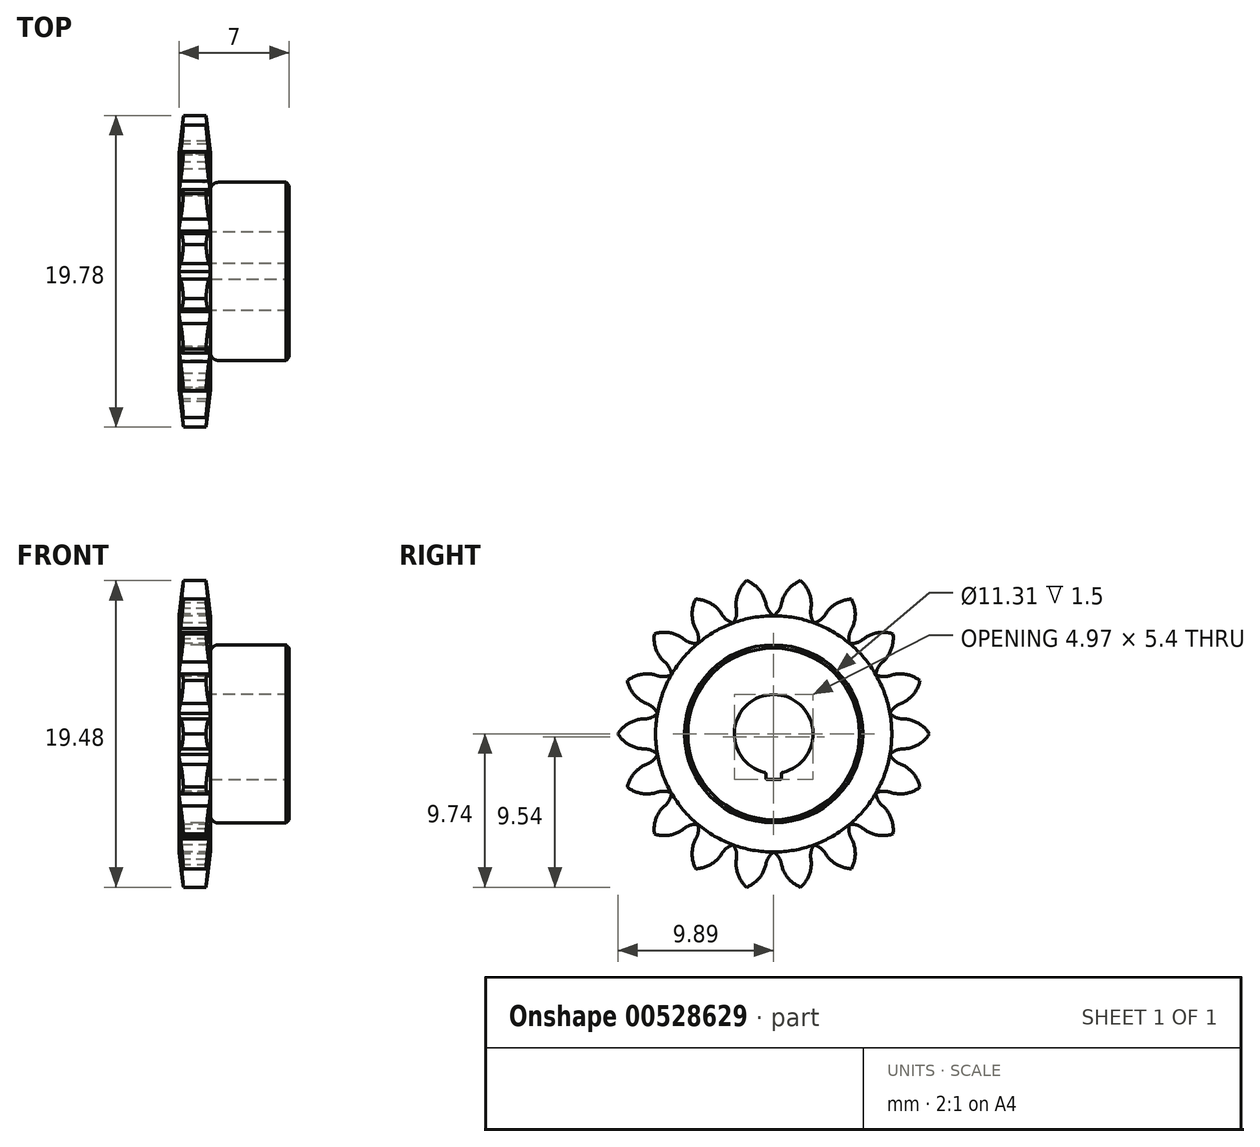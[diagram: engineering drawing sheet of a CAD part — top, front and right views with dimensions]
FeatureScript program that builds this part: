
annotation { "Feature Type Name" : "Feature", "Feature Type Description" : "" }
export const myFeature = defineFeature(function(context is Context, id is Id, definition is map)
    precondition{}
    {
        {
            var Q0;
            Q0=qCreatedBy(makeId("Front.planeOp"),FACE);
            var sketch = newSketch(context, id + "F0", { "sketchPlane" : qUnion([Q0])});
            skLineSegment(sketch, "E0", {"start": v(0, 0) * mm, "end": v(21.65, 0) * mm, "construction": true});
            skLineSegment(sketch, "E1.bottom", {"start": v(0, 10) * mm, "end": v(2, 10) * mm});
            skLineSegment(sketch, "E1.top", {"start": v(0, 2.5) * mm, "end": v(2, 2.5) * mm});
            skLineSegment(sketch, "E1.left", {"start": v(0, 10) * mm, "end": v(0, 2.5) * mm});
            skLineSegment(sketch, "E1.right", {"start": v(2, 10) * mm, "end": v(2, 2.5) * mm});
            skLineSegment(sketch, "E2.bottom", {"start": v(0, 2.5) * mm, "end": v(7, 2.5) * mm});
            skLineSegment(sketch, "E2.top", {"start": v(0, 5.66) * mm, "end": v(7, 5.66) * mm});
            skLineSegment(sketch, "E2.left", {"start": v(0, 2.5) * mm, "end": v(0, 5.66) * mm});
            skLineSegment(sketch, "E2.right", {"start": v(7, 2.5) * mm, "end": v(7, 5.66) * mm});
            skSolve(sketch);
        }
        {
            var Q0;
            {var subQ0=sQuery(id+"F0.wireOp",EDGE,"E1.bottom");Q0=makeQuery(id+"F0.imprint","IMPRINT",FACE,{"disambiguationData":[TD([[makeQuery(id+"F0.imprint","IMPRINT",EDGE,{"derivedFrom":subQ0}),-1.0]])]});}
            var Q1;
            {var subQ5=sQuery(id+"F0.wireOp",EDGE,"E2.right");Q1=makeQuery(id+"F0.imprint","IMPRINT",FACE,{"disambiguationData":[TD([[makeQuery(id+"F0.imprint","IMPRINT",EDGE,{"derivedFrom":subQ5}),1.0]])]});}
            var Q2;
            {var subQ5=sQuery(id+"F0.wireOp",EDGE,"E2.left");Q2=makeQuery(id+"F0.imprint","IMPRINT",FACE,{"disambiguationData":[TD([[makeQuery(id+"F0.imprint","IMPRINT",EDGE,{"derivedFrom":subQ5}),-1.0]])]});}
            var Q3;
            Q3=sQuery(id+"F0.wireOp",EDGE,"E0");
            revolve(context, id + "F1", {"entities" : qUnion([Q0, Q1, Q2]), "axis" : qUnion([Q3]), "revolveType" : RevolveType.FULL});
        }
        {
            var Q0;
            Q0=makeQuery(id+"F1.opRevolve","SWEPT_EDGE",EDGE,{"disambiguationData":[OSD([sQuery(id+"F0.wireOp",EDGE,"E1.right"),sQuery(id+"F0.wireOp",EDGE,"E2.top")])]});
            fillet(context, id + "F2", {"entities" : qUnion([Q0]), "radius" : .5 * mm, "tangentPropagation" : true, "allowEdgeOverflow" : false});
        }
        {
            var Q0;
            Q0=makeQuery(id+"F1.opRevolve","SWEPT_EDGE",EDGE,{"disambiguationData":[OSD([sQuery(id+"F0.wireOp",EDGE,"E2.top"),sQuery(id+"F0.wireOp",EDGE,"E2.right")])]});
            chamfer(context, id + "F3", {"entities" : qUnion([Q0]), "width" : .2 * mm, "tangentPropagation" : true});
        }
        {
            var Q0;
            Q0=makeQuery(id+"F1.opRevolve","SWEPT_EDGE",EDGE,{"disambiguationData":[OSD([sQuery(id+"F0.wireOp",EDGE,"E1.bottom"),sQuery(id+"F0.wireOp",EDGE,"E1.right")])]});
            var Q1;
            Q1=makeQuery(id+"F1.opRevolve","SWEPT_EDGE",EDGE,{"disambiguationData":[OSD([sQuery(id+"F0.wireOp",EDGE,"E1.bottom"),sQuery(id+"F0.wireOp",EDGE,"E1.left")])]});
            chamfer(context, id + "F4", {"entities" : qUnion([Q0, Q1]), "chamferType" : ChamferType.TWO_OFFSETS, "width1" : 2.5 * mm, "oppositeDirection" : true, "width2" : .3 * mm, "tangentPropagation" : true});
        }
        {
            var Q0;
            Q0=qCreatedBy(makeId("Right.planeOp"),FACE);
            var sketch = newSketch(context, id + "F5", { "sketchPlane" : qUnion([Q0])});
            skArc(sketch, "E3", {"start": v(0, 7.5) * mm, "mid": v(0.33, 7.85) * mm, "end": v(0.5, 8.3) * mm});
            skArc(sketch, "E4", {"start": v(1.94, 9.81) * mm, "mid": v(1, 9.26) * mm, "end": v(0.5, 8.3) * mm});
            skArc(sketch, "E5.MirrorCS", {"start": v(0, 7.5) * mm, "mid": v(-0.33, 7.85) * mm, "end": v(-0.5, 8.3) * mm});
            skArc(sketch, "E6.MirrorCS", {"start": v(-1.94, 9.81) * mm, "mid": v(-1, 9.26) * mm, "end": v(-0.5, 8.3) * mm});
            skArc(sketch, "E7", {"start": v(1.94, 9.81) * mm, "mid": v(0, 10.08) * mm, "end": v(-1.94, 9.81) * mm});
            skSolve(sketch);
        }
        {
            var Q0;
            Q0=makeQuery(id+"F5.imprint","IMPRINT",FACE,{"disambiguationData":[TD([[makeQuery(id+"F5.imprint","IMPRINT",EDGE,{"derivedFrom":sQuery(id+"F5.wireOp",EDGE,"B795m6G2-eEBe-JvFf-UA23-ThgfQlkMzyw7")}),1.0]])]});
            var Q1;
            Q1=makeQuery(id+"F5.imprint","IMPRINT",FACE,{"disambiguationData":[TD([[makeQuery(id+"F5.imprint","IMPRINT",EDGE,{"derivedFrom":sQuery(id+"F5.wireOp",EDGE,"E3")}),1.0]])]});
            extrude(context, id + "F6", {"entities" : qUnion([Q0, Q1]), "depth" : 2 * mm, "offsetDistance" : 25 * mm});
        }
        {
            var Q0;
            Q0=makeQuery(id+"F6.opExtrude","SWEPT_BODY",BODY,{"disambiguationData":[OSD([sQuery(id+"F5.wireOp",EDGE,"E3"),sQuery(id+"F5.wireOp",EDGE,"E4"),sQuery(id+"F5.wireOp",EDGE,"E5.MirrorCS"),sQuery(id+"F5.wireOp",EDGE,"E6.MirrorCS"),sQuery(id+"F5.wireOp",EDGE,"E7")])]});
            var Q1;
            {var subQ0=sQuery(id+"F0.wireOp",EDGE,"E1.left");Q1=makeQuery(id+"F4.opChamfer","BLEND_EDGE",EDGE,{"blendedFrom":[makeQuery(id+"F1.opRevolve","SWEPT_EDGE",EDGE,{"disambiguationData":[OSD([sQuery(id+"F0.wireOp",EDGE,"E1.bottom"),subQ0])]}),makeQuery(id+"F1.opRevolve","SWEPT_FACE",FACE,{"disambiguationData":[OSD([subQ0,sQuery(id+"F0.wireOp",EDGE,"E2.left")])]})],"blendedInto":[makeQuery(id+"F1.opRevolve","SWEPT_FACE",FACE,{"disambiguationData":[OSD([subQ0,sQuery(id+"F0.wireOp",EDGE,"E2.left")])]})]});}
            circularPattern(context, id + "F7", {"operationType" : NewBodyOperationType.REMOVE, "entities" : qUnion([Q0]), "axis" : qUnion([Q1]), "angle" : 360 * degree, "instanceCount" : 18, "equalSpace" : true});
        }
        {
            var Q0;
            Q0=makeQuery(id+"F1.opRevolve","SWEPT_FACE",FACE,{"disambiguationData":[OSD([sQuery(id+"F0.wireOp",EDGE,"E2.right")])]});
            var sketch = newSketch(context, id + "F8", { "sketchPlane" : qUnion([Q0])});
            skLineSegment(sketch, "E8.bottom", {"start": v(0.5, -2.9) * mm, "end": v(-0.5, -2.9) * mm});
            skLineSegment(sketch, "E8.top", {"start": v(0.5, -2.1) * mm, "end": v(-0.5, -2.1) * mm});
            skLineSegment(sketch, "E8.left", {"start": v(0.5, -2.9) * mm, "end": v(0.5, -2.1) * mm});
            skLineSegment(sketch, "E8.right", {"start": v(-0.5, -2.9) * mm, "end": v(-0.5, -2.1) * mm});
            skPoint(sketch, "E8.middle", {"position": v(0, -2.5) * mm});
            skSolve(sketch);
        }
        {
            var Q0;
            Q0 = qSketchRegion(id + "F8", true);
            extrude(context, id + "F9", {"entities" : qUnion([Q0]), "operationType" : NewBodyOperationType.REMOVE, "oppositeDirection" : true, "depth" : 25 * mm, "offsetDistance" : 25 * mm});
        }
        {
            var Q0;
            Q0=makeQuery(id+"F9.boolean.opBoolean","COPY",EDGE,{"derivedFrom":makeQuery(id+"F9.opExtrude","SWEPT_EDGE",EDGE,{"disambiguationData":[OSD([sQuery(id+"F8.wireOp",EDGE,"E8.bottom"),sQuery(id+"F8.wireOp",EDGE,"E8.right")])]})});
            var Q1;
            Q1=makeQuery(id+"F9.boolean.opBoolean","COPY",EDGE,{"derivedFrom":makeQuery(id+"F9.opExtrude","SWEPT_EDGE",EDGE,{"disambiguationData":[OSD([sQuery(id+"F8.wireOp",EDGE,"E8.bottom"),sQuery(id+"F8.wireOp",EDGE,"E8.left")])]})});
            var Q2;
            Q2=makeQuery(id+"F9.boolean.opBoolean","INTERSECT",EDGE,{"derivedFrom":[makeQuery(id+"F1.opRevolve","SWEPT_FACE",FACE,{"disambiguationData":[OSD([sQuery(id+"F0.wireOp",EDGE,"E2.bottom")])]}),makeQuery(id+"F9.opExtrude","SWEPT_FACE",FACE,{"disambiguationData":[OSD([sQuery(id+"F8.wireOp",EDGE,"E8.right")])]})]});
            var Q3;
            Q3=makeQuery(id+"F9.boolean.opBoolean","INTERSECT",EDGE,{"derivedFrom":[makeQuery(id+"F1.opRevolve","SWEPT_FACE",FACE,{"disambiguationData":[OSD([sQuery(id+"F0.wireOp",EDGE,"E2.bottom")])]}),makeQuery(id+"F9.opExtrude","SWEPT_FACE",FACE,{"disambiguationData":[OSD([sQuery(id+"F8.wireOp",EDGE,"E8.left")])]})]});
            fillet(context, id + "F10", {"entities" : qUnion([Q0, Q1, Q2, Q3]), "radius" : .1 * mm, "tangentPropagation" : true, "allowEdgeOverflow" : false});
        }
    });
